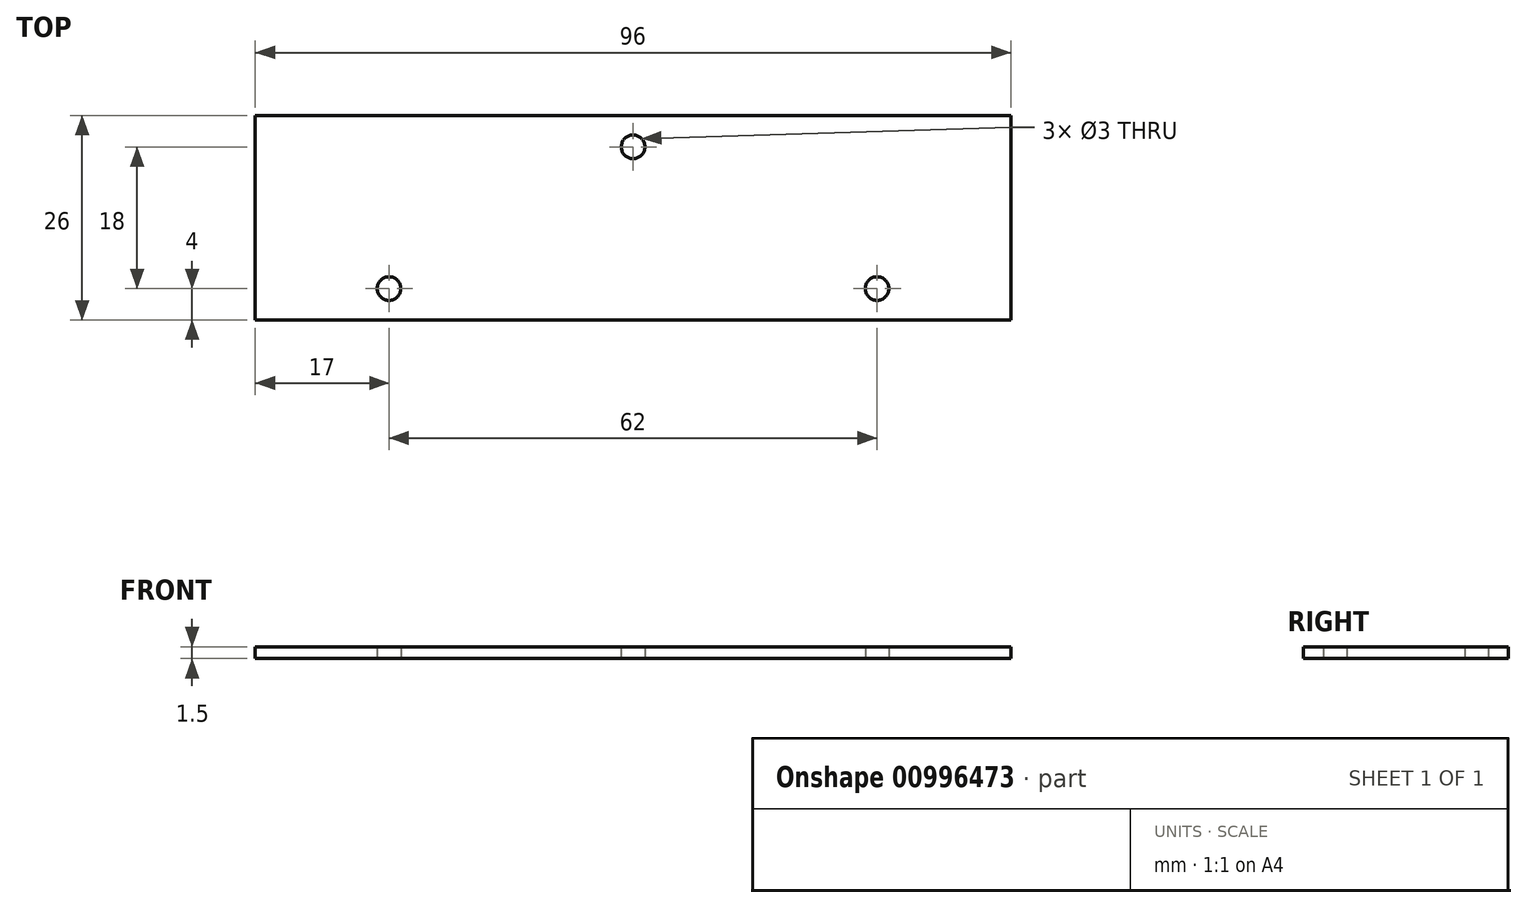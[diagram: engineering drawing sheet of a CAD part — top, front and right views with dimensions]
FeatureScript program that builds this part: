
annotation { "Feature Type Name" : "Feature", "Feature Type Description" : "" }
export const myFeature = defineFeature(function(context is Context, id is Id, definition is map)
    precondition{}
    {
        {
            var Q0;
            Q0=qCreatedBy(makeId("Top.planeOp"),FACE);
            var sketch = newSketch(context, id + "F0", { "sketchPlane" : qUnion([Q0])});
            skLineSegment(sketch, "E0.bottom", {"start": v(-48, -13) * mm, "end": v(48, -13) * mm});
            skLineSegment(sketch, "E0.top", {"start": v(-48, 13) * mm, "end": v(48, 13) * mm});
            skLineSegment(sketch, "E0.left", {"start": v(-48, -13) * mm, "end": v(-48, 13) * mm});
            skLineSegment(sketch, "E0.right", {"start": v(48, -13) * mm, "end": v(48, 13) * mm});
            skLineSegment(sketch, "E1", {"start": v(0, 13) * mm, "end": v(0, -13) * mm, "construction": true});
            skCircle(sketch, "E2", {"center": v(-31, -9) * mm, "radius": 1.5 * mm});
            skCircle(sketch, "E3", {"center": v(31, -9) * mm, "radius": 1.5 * mm});
            skCircle(sketch, "E4", {"center": v(0, 9) * mm, "radius": 1.5 * mm});
            skSolve(sketch);
        }
        {
            var Q0;
            Q0=makeQuery(id+"F0.imprint","IMPRINT",FACE,{"disambiguationData":[TD([[makeQuery(id+"F0.imprint","IMPRINT",EDGE,{"derivedFrom":sQuery(id+"F0.wireOp",EDGE,"E0.bottom")}),1.0]])]});
            extrude(context, id + "F1", {"entities" : qUnion([Q0]), "depth" : 1.5 * mm, "offsetDistance" : 25 * mm});
        }
    });
